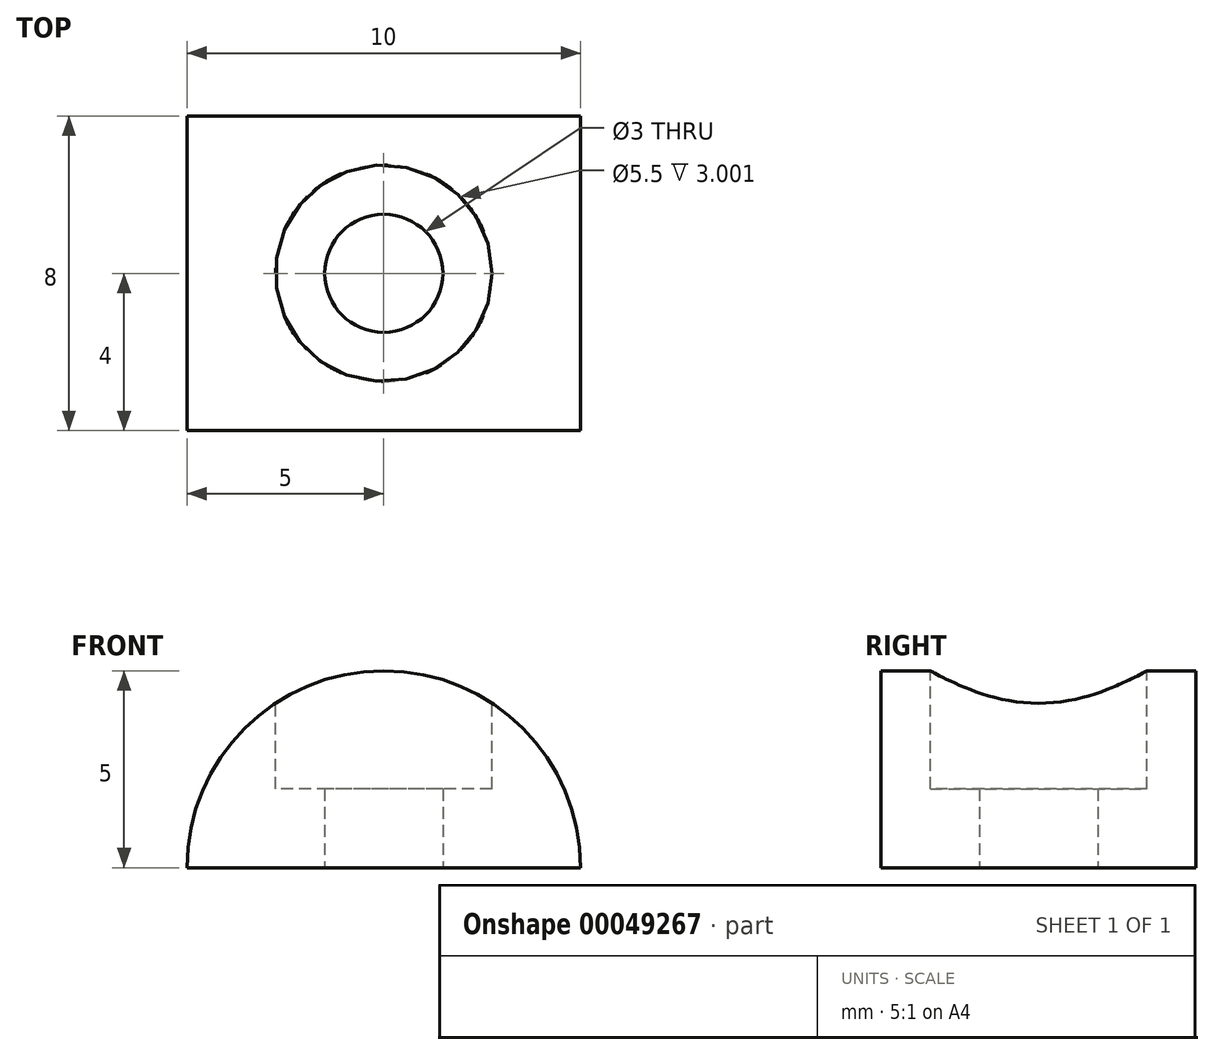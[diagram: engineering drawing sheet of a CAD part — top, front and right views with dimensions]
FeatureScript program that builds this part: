
annotation { "Feature Type Name" : "Feature", "Feature Type Description" : "" }
export const myFeature = defineFeature(function(context is Context, id is Id, definition is map)
    precondition{}
    {
        {
            var Q0;
            Q0=qCreatedBy(makeId("Top.planeOp"),FACE);
            var sketch = newSketch(context, id + "F0", { "sketchPlane" : qUnion([Q0])});
            skLineSegment(sketch, "E0.bottom", {"start": v(0, 0) * mm, "end": v(10, 0) * mm});
            skLineSegment(sketch, "E0.top", {"start": v(0, 8) * mm, "end": v(10, 8) * mm});
            skLineSegment(sketch, "E0.left", {"start": v(0, 0) * mm, "end": v(0, 8) * mm});
            skLineSegment(sketch, "E0.right", {"start": v(10, 0) * mm, "end": v(10, 8) * mm});
            skSolve(sketch);
        }
        {
            var Q0;
            Q0=makeQuery(id+"F0.imprint","IMPRINT",FACE,{"disambiguationData":[TD([[makeQuery(id+"F0.imprint","IMPRINT",EDGE,{"derivedFrom":sQuery(id+"F0.wireOp",EDGE,"E0.bottom")}),1.0]])]});
            extrude(context, id + "F1", {"entities" : qUnion([Q0]), "depth" : 5 * mm});
        }
        {
            var Q0;
            Q0=makeQuery(id+"F1.opExtrude","CAP_EDGE",EDGE,{"disambiguationData":[OSD([sQuery(id+"F0.wireOp",EDGE,"E0.left")])],"isStart":false});
            var Q1;
            Q1=makeQuery(id+"F1.opExtrude","CAP_EDGE",EDGE,{"disambiguationData":[OSD([sQuery(id+"F0.wireOp",EDGE,"E0.right")])],"isStart":false});
            fillet(context, id + "F2", {"entities" : qUnion([Q0, Q1]), "radius" : 5 * mm, "tangentPropagation" : true, "allowEdgeOverflow" : false});
        }
        {
            var Q0;
            Q0=makeQuery(id+"F1.opExtrude","CAP_FACE",FACE,{"disambiguationData":[OSD([sQuery(id+"F0.wireOp",EDGE,"E0.bottom"),sQuery(id+"F0.wireOp",EDGE,"E0.top"),sQuery(id+"F0.wireOp",EDGE,"E0.left"),sQuery(id+"F0.wireOp",EDGE,"E0.right")])],"isStart":true});
            var sketch = newSketch(context, id + "F3", { "sketchPlane" : qUnion([Q0])});
            skCircle(sketch, "E1", {"center": v(5, -4) * mm, "radius": 2.75 * mm});
            skCircle(sketch, "E2", {"center": v(5, -4) * mm, "radius": 1.5 * mm});
            skSolve(sketch);
        }
        {
            var Q0;
            Q0=qCreatedBy(makeId("Top.planeOp"),FACE);
            cPlane(context, id + "F4", {"entities" : qUnion([Q0]), "cplaneType" : CPlaneType.OFFSET, "offset" : 5 * mm, "width" : 150 * mm, "height" : 150 * mm});
        }
        {
            var Q0;
            Q0=makeQuery(id+"F3.imprint","IMPRINT",FACE,{"disambiguationData":[TD([[makeQuery(id+"F3.imprint","IMPRINT",EDGE,{"derivedFrom":sQuery(id+"F3.wireOp",EDGE,"E2")}),1.0]])]});
            var Q1;
            Q1=sQuery(id+"F3.wireOp",EDGE,"E2");
            extrude(context, id + "F5", {"entities" : qUnion([Q0]), "operationType" : NewBodyOperationType.REMOVE, "surfaceEntities" : qUnion([Q1]), "oppositeDirection" : true, "depth" : 5 * mm});
        }
        {
            var Q0;
            Q0=qCreatedBy(id+"F4.planeOp",FACE);
            var sketch = newSketch(context, id + "F6", { "sketchPlane" : qUnion([Q0])});
            skCircle(sketch, "E3", {"center": v(5, 4) * mm, "radius": 2.75 * mm});
            skSolve(sketch);
        }
        {
            var Q0;
            Q0 = qSketchRegion(id + "F6", true);
            extrude(context, id + "F7", {"entities" : qUnion([Q0]), "operationType" : NewBodyOperationType.REMOVE, "oppositeDirection" : true, "depth" : 3 * mm});
        }
    });
